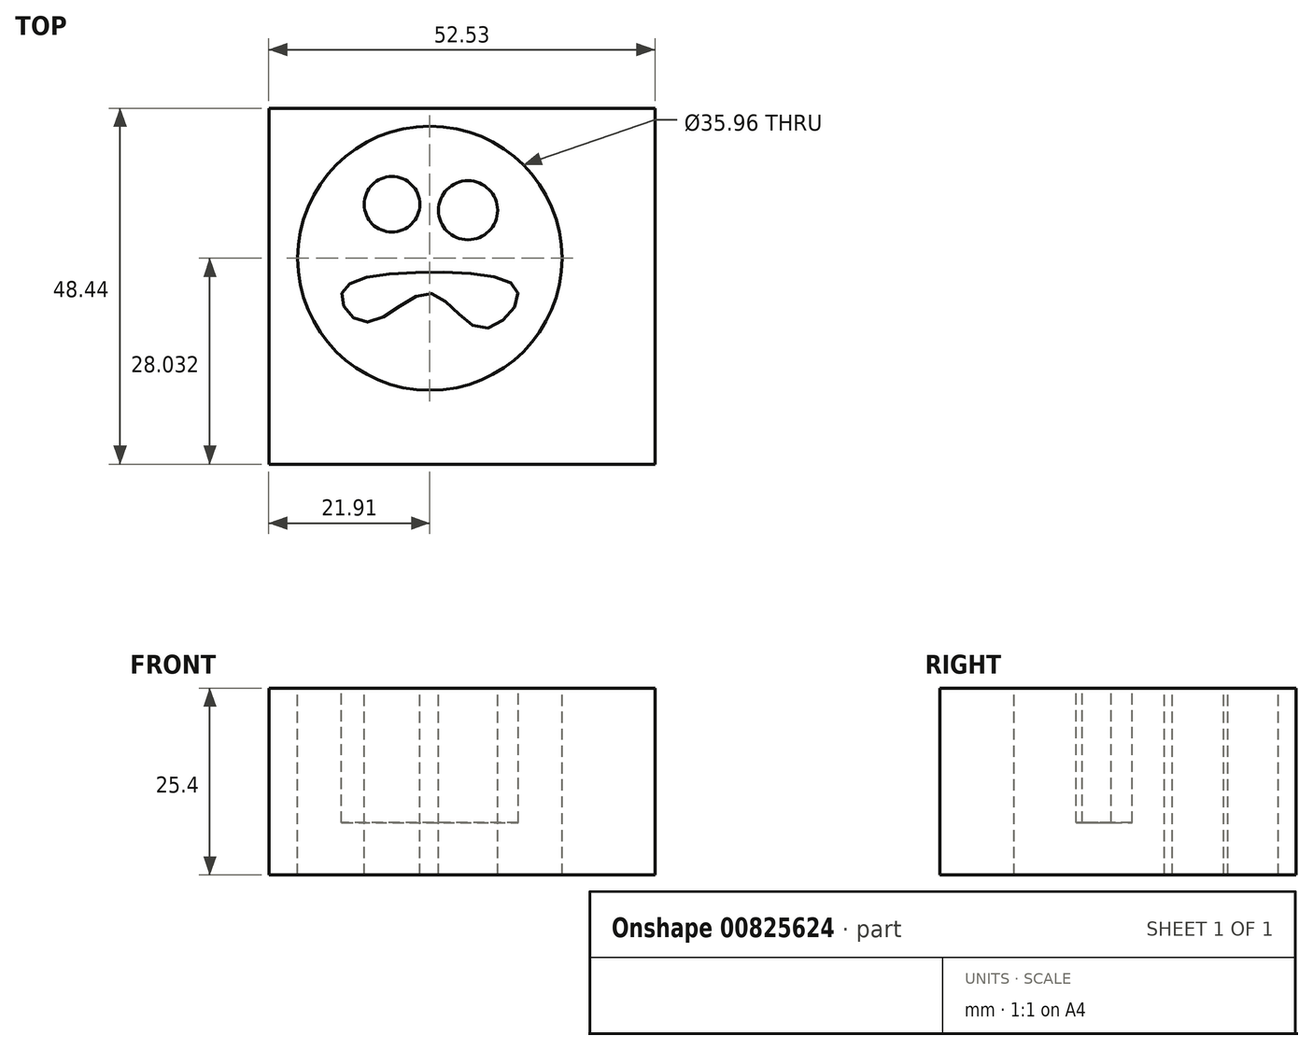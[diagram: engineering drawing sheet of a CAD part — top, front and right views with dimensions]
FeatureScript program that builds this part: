
annotation { "Feature Type Name" : "Feature", "Feature Type Description" : "" }
export const myFeature = defineFeature(function(context is Context, id is Id, definition is map)
    precondition{}
    {
        {
            var Q0;
            Q0=qCreatedBy(makeId("Top.planeOp"),FACE);
            var sketch = newSketch(context, id + "F0", { "sketchPlane" : qUnion([Q0])});
            skLineSegment(sketch, "E0.bottom", {"start": v(-21.9, 25.17) * mm, "end": v(30.62, 25.17) * mm});
            skLineSegment(sketch, "E0.top", {"start": v(-21.9, -23.27) * mm, "end": v(30.62, -23.27) * mm});
            skLineSegment(sketch, "E0.left", {"start": v(-21.9, 25.17) * mm, "end": v(-21.9, -23.27) * mm});
            skLineSegment(sketch, "E0.right", {"start": v(30.62, 25.17) * mm, "end": v(30.62, -23.27) * mm});
            skSolve(sketch);
        }
        {
            var Q0;
            Q0=makeQuery(id+"F0.imprint","IMPRINT",FACE,{"disambiguationData":[TD([[makeQuery(id+"F0.imprint","IMPRINT",EDGE,{"derivedFrom":sQuery(id+"F0.wireOp",EDGE,"E0.bottom")}),-1.0]])]});
            extrude(context, id + "F1", {"entities" : qUnion([Q0]), "depth" : 25.4 * mm, "offsetDistance" : 25.4 * mm});
        }
        {
            var Q0;
            Q0=makeQuery(id+"F1.opExtrude","CAP_FACE",FACE,{"disambiguationData":[OSD([sQuery(id+"F0.wireOp",EDGE,"E0.bottom"),sQuery(id+"F0.wireOp",EDGE,"E0.top"),sQuery(id+"F0.wireOp",EDGE,"E0.left"),sQuery(id+"F0.wireOp",EDGE,"E0.right")])],"isStart":false});
            var sketch = newSketch(context, id + "F2", { "sketchPlane" : qUnion([Q0])});
            skCircle(sketch, "E1", {"center": v(0, 4.76) * mm, "radius": 17.98 * mm});
            skSolve(sketch);
        }
        {
            var Q0;
            Q0=makeQuery(id+"F2.imprint","IMPRINT",FACE,{"disambiguationData":[TD([[makeQuery(id+"F2.imprint","IMPRINT",EDGE,{"derivedFrom":sQuery(id+"F2.wireOp",EDGE,"E1")}),1.0]])]});
            var sketch = newSketch(context, id + "F3", { "sketchPlane" : qUnion([Q0])});
            skCircle(sketch, "E2", {"center": v(-5.15, 12.11) * mm, "radius": 3.78 * mm});
            skCircle(sketch, "E3", {"center": v(5.19, 11.3) * mm, "radius": 4.02 * mm});
            skSolve(sketch);
        }
        {
            var Q0;
            Q0=makeQuery(id+"F2.imprint","IMPRINT",FACE,{"disambiguationData":[TD([[makeQuery(id+"F2.imprint","IMPRINT",EDGE,{"derivedFrom":sQuery(id+"F2.wireOp",EDGE,"E1")}),1.0]])]});
            var sketch = newSketch(context, id + "F4", { "sketchPlane" : qUnion([Q0])});
            skFitSpline(sketch, "E4", {"points": [v(-11.96, 0) * mm, v(0, 2.86) * mm, v(12, 0) * mm, v(7.1, -4.76) * mm, v(0, 0) * mm, v(-8.69, -3.95) * mm, v(-11.96, 0) * mm]});
            skSolve(sketch);
        }
        {
            var Q0;
            Q0=sQuery(id+"F2.wireOp",EDGE,"E1");
            extrude(context, id + "F5", {"bodyType" : ToolBodyType.SURFACE, "surfaceEntities" : qUnion([Q0]), "oppositeDirection" : true, "depth" : 23.37 * mm, "offsetDistance" : 25.4 * mm});
        }
        {
            var Q0;
            Q0=makeQuery(id+"F3.imprint","IMPRINT",FACE,{"disambiguationData":[TD([[makeQuery(id+"F3.imprint","IMPRINT",EDGE,{"derivedFrom":sQuery(id+"F3.wireOp",EDGE,"E2")}),-1.0]])]});
            extrude(context, id + "F6", {"entities" : qUnion([Q0]), "operationType" : NewBodyOperationType.REMOVE, "oppositeDirection" : true, "depth" : 27.43 * mm, "offsetDistance" : 25.4 * mm});
        }
        {
            var Q0;
            Q0=makeQuery(id+"F4.imprint","IMPRINT",FACE,{"disambiguationData":[TD([[makeQuery(id+"F4.imprint","IMPRINT",EDGE,{"derivedFrom":sQuery(id+"F4.wireOp",EDGE,"E4")}),-1.0]])]});
            extrude(context, id + "F7", {"entities" : qUnion([Q0]), "oppositeDirection" : true, "depth" : 18.29 * mm, "offsetDistance" : 25.4 * mm});
        }
    });
